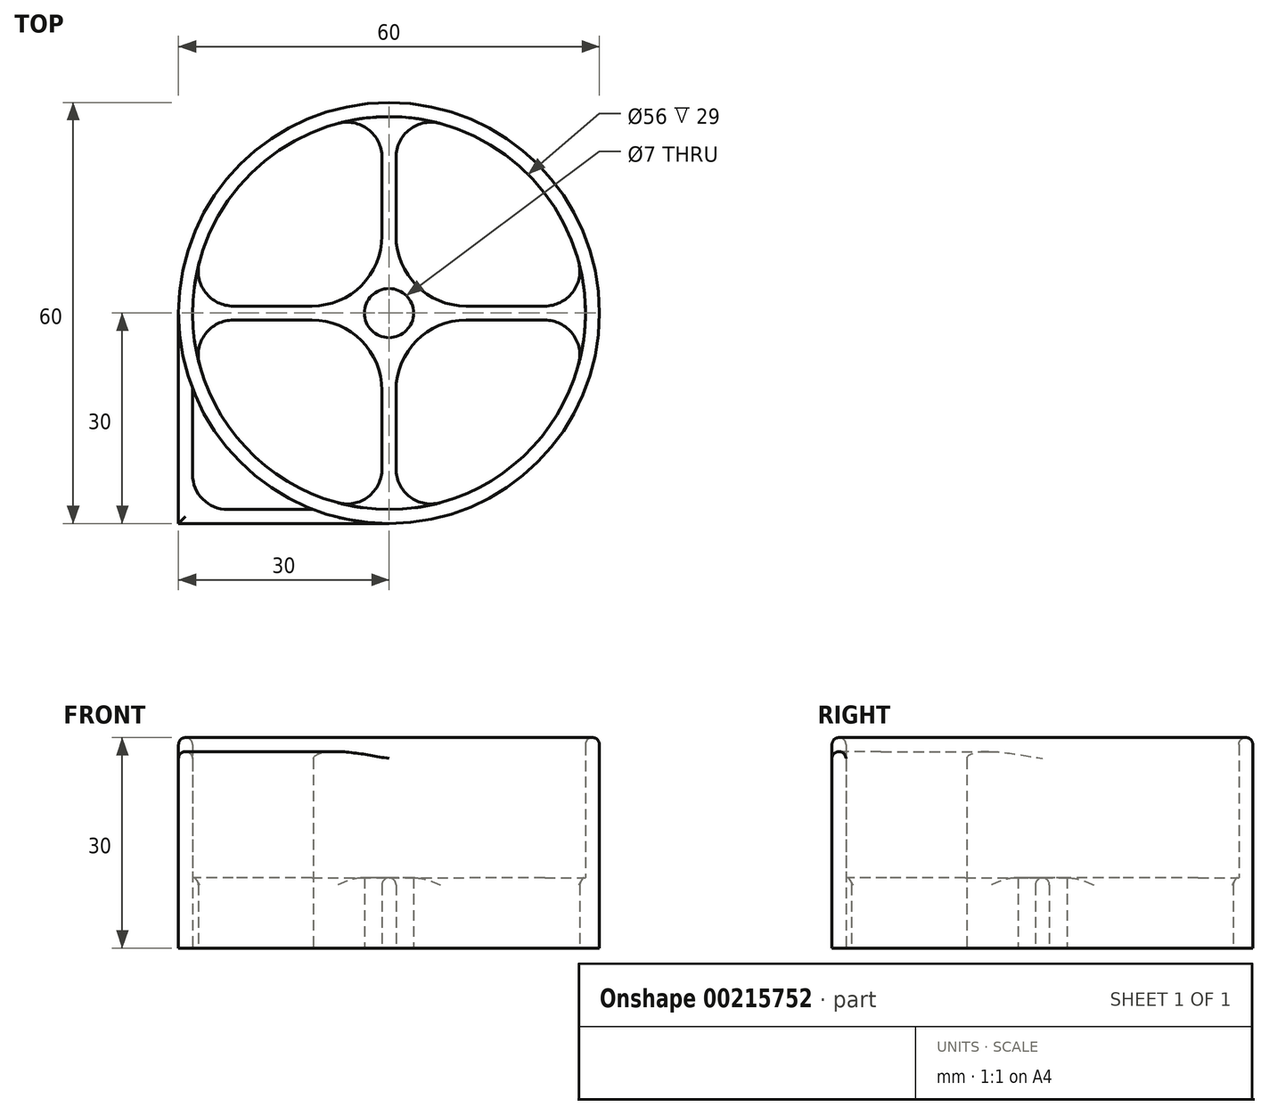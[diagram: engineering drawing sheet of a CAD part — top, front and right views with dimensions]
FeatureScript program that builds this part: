
annotation { "Feature Type Name" : "Feature", "Feature Type Description" : "" }
export const myFeature = defineFeature(function(context is Context, id is Id, definition is map)
    precondition{}
    {
        {
            var Q0;
            Q0=qCreatedBy(makeId("Top.planeOp"),FACE);
            var sketch = newSketch(context, id + "F0", { "sketchPlane" : qUnion([Q0])});
            skArc(sketch, "E0", {"start": v(-7.3, 27.03) * mm, "mid": v(-19.8, 19.8) * mm, "end": v(-27.03, 7.3) * mm});
            skCircle(sketch, "E1", {"center": v(0, 0) * mm, "radius": 30 * mm});
            skLineSegment(sketch, "E2.left", {"start": v(1, -22.2) * mm, "end": v(1, -11) * mm});
            skLineSegment(sketch, "E2.right", {"start": v(-1, -22.2) * mm, "end": v(-1, -11) * mm});
            skCircle(sketch, "E3", {"center": v(0, 0) * mm, "radius": 3.5 * mm});
            skLineSegment(sketch, "E4.bottom", {"start": v(22.2, -1) * mm, "end": v(11, -1) * mm});
            skLineSegment(sketch, "E4.top", {"start": v(22.2, 1) * mm, "end": v(11, 1) * mm});
            skLineSegment(sketch, "E5.trimOffspring", {"start": v(-1, 11) * mm, "end": v(-1, 22.2) * mm});
            skLineSegment(sketch, "E6.trimOffspring", {"start": v(1, 11) * mm, "end": v(1, 22.2) * mm});
            skLineSegment(sketch, "E7.trimOffspring", {"start": v(-11, 1) * mm, "end": v(-22.2, 1) * mm});
            skLineSegment(sketch, "E8.trimOffspring", {"start": v(-11, -1) * mm, "end": v(-22.2, -1) * mm});
            skArc(sketch, "E9.filletArc", {"start": v(-11, 1) * mm, "mid": v(-3.93, 3.93) * mm, "end": v(-1, 11) * mm});
            skArc(sketch, "E10.filletArc", {"start": v(1, 11) * mm, "mid": v(3.93, 3.93) * mm, "end": v(11, 1) * mm});
            skArc(sketch, "E11.filletArc", {"start": v(11, -1) * mm, "mid": v(3.93, -3.93) * mm, "end": v(1, -11) * mm});
            skArc(sketch, "E12.filletArc", {"start": v(-1, -11) * mm, "mid": v(-3.93, -3.93) * mm, "end": v(-11, -1) * mm});
            skPoint(sketch, "E2.top.end.orphan", {"position": v(-1, 28.96) * mm});
            skPoint(sketch, "E2.top.start.orphan", {"position": v(1, 28.96) * mm});
            skPoint(sketch, "E13.orphan", {"position": v(-28.88, 1) * mm});
            skPoint(sketch, "E14.orphan", {"position": v(-28.88, -1) * mm});
            skArc(sketch, "E15.trimOffspring", {"start": v(-27.03, -7.3) * mm, "mid": v(-19.8, -19.8) * mm, "end": v(-7.3, -27.03) * mm});
            skArc(sketch, "E16.trimOffspring", {"start": v(27.03, 7.3) * mm, "mid": v(19.8, 19.8) * mm, "end": v(7.3, 27.03) * mm});
            skPoint(sketch, "E4.left.end.orphan", {"position": v(28.88, 1) * mm});
            skPoint(sketch, "E17.orphan", {"position": v(28.88, -1) * mm});
            skArc(sketch, "E18.trimOffspring", {"start": v(7.3, -27.03) * mm, "mid": v(19.8, -19.8) * mm, "end": v(27.03, -7.3) * mm});
            skPoint(sketch, "E2.bottom.end.orphan", {"position": v(-1, -28.96) * mm});
            skPoint(sketch, "E19.orphan", {"position": v(1, -28.96) * mm});
            skPoint(sketch, "E20.visualSharp", {"position": v(1, 27.98) * mm});
            skArc(sketch, "E20.filletArc", {"start": v(7.3, 27.03) * mm, "mid": v(2.96, 26.17) * mm, "end": v(1, 22.2) * mm});
            skPoint(sketch, "E21.visualSharp", {"position": v(-1, 27.98) * mm});
            skArc(sketch, "E21.filletArc", {"start": v(-1, 22.2) * mm, "mid": v(-2.96, 26.17) * mm, "end": v(-7.3, 27.03) * mm});
            skPoint(sketch, "E22.visualSharp", {"position": v(-27.98, 1) * mm});
            skArc(sketch, "E22.filletArc", {"start": v(-27.03, 7.3) * mm, "mid": v(-26.17, 2.96) * mm, "end": v(-22.2, 1) * mm});
            skPoint(sketch, "E23.visualSharp", {"position": v(-27.98, -1) * mm});
            skArc(sketch, "E23.filletArc", {"start": v(-22.2, -1) * mm, "mid": v(-26.17, -2.96) * mm, "end": v(-27.03, -7.3) * mm});
            skPoint(sketch, "E24.visualSharp", {"position": v(27.98, 1) * mm});
            skArc(sketch, "E24.filletArc", {"start": v(22.2, 1) * mm, "mid": v(26.17, 2.96) * mm, "end": v(27.03, 7.3) * mm});
            skPoint(sketch, "E25.visualSharp", {"position": v(27.98, -1) * mm});
            skArc(sketch, "E25.filletArc", {"start": v(27.03, -7.3) * mm, "mid": v(26.17, -2.96) * mm, "end": v(22.2, -1) * mm});
            skPoint(sketch, "E26.visualSharp", {"position": v(-1, -27.98) * mm});
            skArc(sketch, "E26.filletArc", {"start": v(-7.3, -27.03) * mm, "mid": v(-2.96, -26.17) * mm, "end": v(-1, -22.2) * mm});
            skPoint(sketch, "E27.visualSharp", {"position": v(1, -27.98) * mm});
            skArc(sketch, "E27.filletArc", {"start": v(1, -22.2) * mm, "mid": v(2.96, -26.17) * mm, "end": v(7.3, -27.03) * mm});
            skLineSegment(sketch, "E28", {"start": v(-30, 0) * mm, "end": v(-30, -30) * mm});
            skLineSegment(sketch, "E29", {"start": v(-30, -30) * mm, "end": v(0, -30) * mm});
            skLineSegment(sketch, "E30", {"start": v(-28, -10.77) * mm, "end": v(-28, -23) * mm});
            skLineSegment(sketch, "E31", {"start": v(-23, -28) * mm, "end": v(-10.77, -28) * mm});
            skPoint(sketch, "E32.visualSharp", {"position": v(-28, -28) * mm});
            skArc(sketch, "E32.filletArc", {"start": v(-28, -23) * mm, "mid": v(-26.54, -26.54) * mm, "end": v(-23, -28) * mm});
            skCircle(sketch, "E33", {"center": v(0, 0) * mm, "radius": 28 * mm});
            skSolve(sketch);
        }
        {
            var Q0;
            {var subQ7=sQuery(id+"F0.wireOp",EDGE,"E1");var subQ8=makeQuery(id+"F0.imprint","INTERSECT",VERTEX,{"derivedFrom":[subQ7,sQuery(id+"F0.wireOp",EDGE,"E28")]});Q0=makeQuery(id+"F0.imprint","IMPRINT",FACE,{"disambiguationData":[TD([[makeQuery(id+"F0.imprint","IMPRINT",EDGE,{"disambiguationData":[TD([[subQ8,-1.0]])],"derivedFrom":subQ7}),1.0]])]});}
            extrude(context, id + "F1", {"entities" : qUnion([Q0]), "depth" : 30 * mm});
        }
        {
            var Q0;
            Q0=makeQuery(id+"F0.imprint","IMPRINT",FACE,{"disambiguationData":[TD([[makeQuery(id+"F0.imprint","IMPRINT",EDGE,{"derivedFrom":sQuery(id+"F0.wireOp",EDGE,"E2.left")}),1.0]])]});
            extrude(context, id + "F2", {"entities" : qUnion([Q0]), "operationType" : NewBodyOperationType.ADD, "depth" : 10 * mm});
        }
        {
            var Q0;
            {var subQ1=sQuery(id+"F0.wireOp",EDGE,"E28");Q0=makeQuery(id+"F0.imprint","IMPRINT",FACE,{"disambiguationData":[TD([[makeQuery(id+"F0.imprint","IMPRINT",EDGE,{"derivedFrom":subQ1}),1.0]])]});}
            extrude(context, id + "F3", {"entities" : qUnion([Q0]), "operationType" : NewBodyOperationType.ADD, "depth" : 28 * mm});
        }
        {
            var Q0;
            Q0=makeQuery(id+"F1.opExtrude","CAP_FACE",FACE,{"disambiguationData":[OSD([sQuery(id+"F0.wireOp",EDGE,"E1"),sQuery(id+"F0.wireOp",EDGE,"E33")])],"isStart":false});
            fillet(context, id + "F4", {"entities" : qUnion([Q0]), "radius" : 1 * mm, "tangentPropagation" : true, "allowEdgeOverflow" : false});
        }
        {
            var Q0;
            Q0=makeQuery(id+"F3.opExtrude","CAP_EDGE",EDGE,{"disambiguationData":[OSD([sQuery(id+"F0.wireOp",EDGE,"E29")])],"isStart":false});
            var Q1;
            Q1=makeQuery(id+"F3.opExtrude","CAP_EDGE",EDGE,{"disambiguationData":[OSD([sQuery(id+"F0.wireOp",EDGE,"E28")])],"isStart":false});
            var Q2;
            Q2=makeQuery(id+"F3.opExtrude","CAP_EDGE",EDGE,{"disambiguationData":[OSD([sQuery(id+"F0.wireOp",EDGE,"E30")])],"isStart":false});
            fillet(context, id + "F5", {"entities" : qUnion([Q0, Q1, Q2]), "radius" : 1 * mm, "tangentPropagation" : true, "allowEdgeOverflow" : false});
        }
        {
            var Q0;
            Q0=makeQuery(id+"F2.opExtrude","CAP_EDGE",EDGE,{"disambiguationData":[OSD([sQuery(id+"F0.wireOp",EDGE,"E4.bottom")])],"isStart":false});
            var Q1;
            Q1=makeQuery(id+"F2.opExtrude","CAP_EDGE",EDGE,{"disambiguationData":[OSD([sQuery(id+"F0.wireOp",EDGE,"E4.top")])],"isStart":false});
            var Q2;
            Q2=makeQuery(id+"F2.opExtrude","CAP_EDGE",EDGE,{"disambiguationData":[OSD([sQuery(id+"F0.wireOp",EDGE,"E2.right")])],"isStart":false});
            var Q3;
            Q3=makeQuery(id+"F2.opExtrude","CAP_EDGE",EDGE,{"disambiguationData":[OSD([sQuery(id+"F0.wireOp",EDGE,"E7.trimOffspring")])],"isStart":false});
            fillet(context, id + "F6", {"entities" : qUnion([Q0, Q1, Q2, Q3]), "radius" : 1 * mm, "tangentPropagation" : true, "allowEdgeOverflow" : false});
        }
    });
